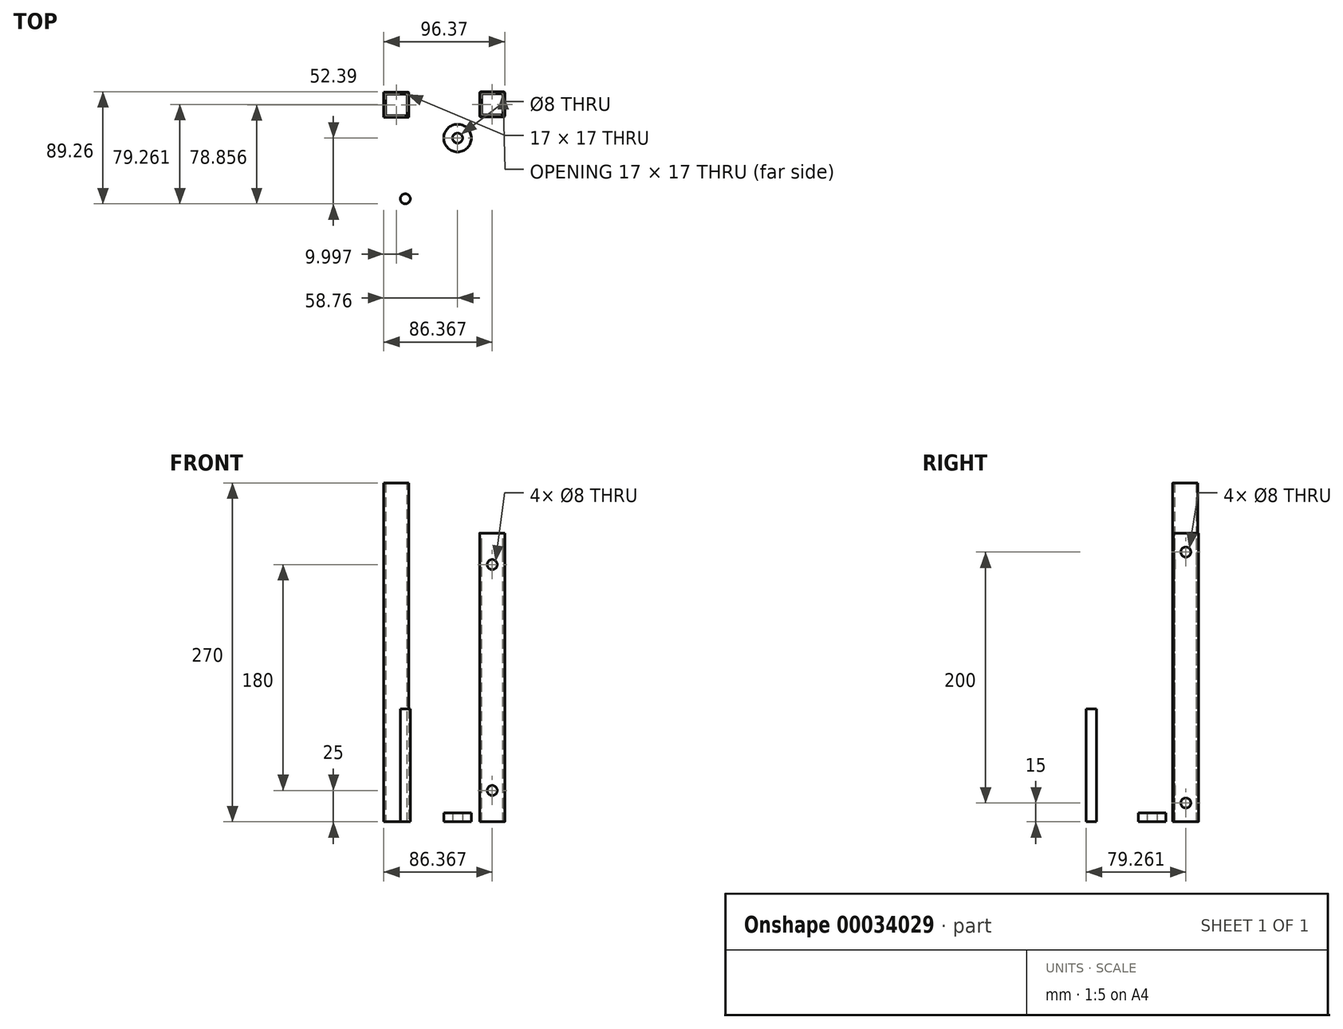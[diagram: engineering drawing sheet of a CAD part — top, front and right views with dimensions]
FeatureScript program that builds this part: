
annotation { "Feature Type Name" : "Feature", "Feature Type Description" : "" }
export const myFeature = defineFeature(function(context is Context, id is Id, definition is map)
    precondition{}
    {
        {
            assignVariable(context, id + "F0", {"name" : "OD1", "anyValue" : 8});
        }
        {
            var Q0;
            Q0=qCreatedBy(makeId("Top.planeOp"),FACE);
            var sketch = newSketch(context, id + "F1", { "sketchPlane" : qUnion([Q0])});
            skCircle(sketch, "E0", {"center": v(0, 0) * mm, "radius": 4 * mm});
            skCircle(sketch, "E1", {"center": v(0, 0) * mm, "radius": 11 * mm});
            skSolve(sketch);
        }
        {
            var Q0;
            Q0 = qSketchRegion(id + "F1", true);
            extrude(context, id + "F2", {"entities" : qUnion([Q0]), "depth" : 7 * mm});
        }
        {
            var Q0;
            Q0=qCreatedBy(makeId("Top.planeOp"),FACE);
            var sketch = newSketch(context, id + "F3", { "sketchPlane" : qUnion([Q0])});
            skLineSegment(sketch, "E2.bottom", {"start": v(-58.76, 36.47) * mm, "end": v(-38.76, 36.47) * mm});
            skLineSegment(sketch, "E2.top", {"start": v(-58.76, 16.47) * mm, "end": v(-38.76, 16.47) * mm});
            skLineSegment(sketch, "E2.left", {"start": v(-58.76, 36.47) * mm, "end": v(-58.76, 16.47) * mm});
            skLineSegment(sketch, "E2.right", {"start": v(-38.76, 36.47) * mm, "end": v(-38.76, 16.47) * mm});
            skSolve(sketch);
        }
        {
            var Q0;
            Q0 = qSketchRegion(id + "F3", true);
            extrude(context, id + "F4", {"entities" : qUnion([Q0]), "depth" : 270 * mm});
        }
        {
            var Q0;
            Q0=makeQuery(id+"F4.opExtrude","SWEPT_EDGE",EDGE,{"disambiguationData":[OSD([sQuery(id+"F3.wireOp",EDGE,"E2.bottom"),sQuery(id+"F3.wireOp",EDGE,"E2.right")])]});
            var Q1;
            Q1=makeQuery(id+"F4.opExtrude","SWEPT_EDGE",EDGE,{"disambiguationData":[OSD([sQuery(id+"F3.wireOp",EDGE,"E2.top"),sQuery(id+"F3.wireOp",EDGE,"E2.right")])]});
            fillet(context, id + "F5", {"entities" : qUnion([Q0, Q1]), "radius" : 0.5 * mm, "tangentPropagation" : true, "allowEdgeOverflow" : false});
        }
        {
            var Q0;
            Q0=makeQuery(id+"F4.opExtrude","CAP_FACE",FACE,{"disambiguationData":[OSD([sQuery(id+"F3.wireOp",EDGE,"E2.bottom"),sQuery(id+"F3.wireOp",EDGE,"E2.top"),sQuery(id+"F3.wireOp",EDGE,"E2.left"),sQuery(id+"F3.wireOp",EDGE,"E2.right")])],"isStart":false});
            var Q1;
            Q1=makeQuery(id+"F4.opExtrude","CAP_FACE",FACE,{"disambiguationData":[OSD([sQuery(id+"F3.wireOp",EDGE,"E2.bottom"),sQuery(id+"F3.wireOp",EDGE,"E2.top"),sQuery(id+"F3.wireOp",EDGE,"E2.left"),sQuery(id+"F3.wireOp",EDGE,"E2.right")])],"isStart":true});
            shell(context, id + "F6", {"entities" : qUnion([Q0, Q1]), "thickness" : 1.5 * mm});
        }
        {
            var Q0;
            Q0=qCreatedBy(makeId("Top.planeOp"),FACE);
            var sketch = newSketch(context, id + "F7", { "sketchPlane" : qUnion([Q0])});
            skLineSegment(sketch, "E3.bottom", {"start": v(17.6, 36.87) * mm, "end": v(37.6, 36.87) * mm});
            skLineSegment(sketch, "E3.top", {"start": v(17.6, 16.87) * mm, "end": v(37.6, 16.87) * mm});
            skLineSegment(sketch, "E3.left", {"start": v(17.6, 36.87) * mm, "end": v(17.6, 16.87) * mm});
            skLineSegment(sketch, "E3.right", {"start": v(37.6, 36.87) * mm, "end": v(37.6, 16.87) * mm});
            skSolve(sketch);
        }
        {
            var Q0;
            Q0 = qSketchRegion(id + "F7", true);
            extrude(context, id + "F8", {"entities" : qUnion([Q0]), "depth" : 230 * mm});
        }
        {
            var Q0;
            Q0=makeQuery(id+"F8.opExtrude","SWEPT_EDGE",EDGE,{"disambiguationData":[OSD([sQuery(id+"F7.wireOp",EDGE,"E3.bottom"),sQuery(id+"F7.wireOp",EDGE,"E3.right")])]});
            var Q1;
            Q1=makeQuery(id+"F8.opExtrude","SWEPT_EDGE",EDGE,{"disambiguationData":[OSD([sQuery(id+"F7.wireOp",EDGE,"E3.bottom"),sQuery(id+"F7.wireOp",EDGE,"E3.left")])]});
            var Q2;
            Q2=makeQuery(id+"F8.opExtrude","SWEPT_EDGE",EDGE,{"disambiguationData":[OSD([sQuery(id+"F7.wireOp",EDGE,"E3.top"),sQuery(id+"F7.wireOp",EDGE,"E3.right")])]});
            var Q3;
            Q3=makeQuery(id+"F8.opExtrude","SWEPT_EDGE",EDGE,{"disambiguationData":[OSD([sQuery(id+"F7.wireOp",EDGE,"E3.top"),sQuery(id+"F7.wireOp",EDGE,"E3.left")])]});
            fillet(context, id + "F9", {"entities" : qUnion([Q0, Q1, Q2, Q3]), "radius" : 1 * mm, "tangentPropagation" : true, "allowEdgeOverflow" : false});
        }
        {
            var Q0;
            Q0=makeQuery(id+"F8.opExtrude","CAP_FACE",FACE,{"disambiguationData":[OSD([sQuery(id+"F7.wireOp",EDGE,"E3.bottom"),sQuery(id+"F7.wireOp",EDGE,"E3.top"),sQuery(id+"F7.wireOp",EDGE,"E3.left"),sQuery(id+"F7.wireOp",EDGE,"E3.right")])],"isStart":false});
            var Q1;
            Q1=makeQuery(id+"F8.opExtrude","CAP_FACE",FACE,{"disambiguationData":[OSD([sQuery(id+"F7.wireOp",EDGE,"E3.bottom"),sQuery(id+"F7.wireOp",EDGE,"E3.top"),sQuery(id+"F7.wireOp",EDGE,"E3.left"),sQuery(id+"F7.wireOp",EDGE,"E3.right")])],"isStart":true});
            shell(context, id + "F10", {"entities" : qUnion([Q0, Q1]), "thickness" : 1.5 * mm});
        }
        {
            var Q0;
            Q0=makeQuery(id+"F8.opExtrude","SWEPT_FACE",FACE,{"disambiguationData":[OSD([sQuery(id+"F7.wireOp",EDGE,"E3.right")])]});
            var sketch = newSketch(context, id + "F11", { "sketchPlane" : qUnion([Q0])});
            skPoint(sketch, "E4", {"position": v(26.87, 215) * mm});
            skPoint(sketch, "E4.positionSnap0", {"position": v(26.87, 230) * mm});
            skPoint(sketch, "E5", {"position": v(26.87, 15) * mm});
            skPoint(sketch, "E5.positionSnap0", {"position": v(26.87, 0) * mm});
            skSolve(sketch);
        }
        {
            var Q0;
            Q0=sQuery(id+"F11.wireOp",VERTEX,"E5");
            var Q1;
            Q1=sQuery(id+"F11.wireOp",VERTEX,"E4");
            var Q2;
            Q2=makeQuery(id+"F8.opExtrude","SWEPT_BODY",BODY,{"disambiguationData":[OSD([sQuery(id+"F7.wireOp",EDGE,"E3.bottom"),sQuery(id+"F7.wireOp",EDGE,"E3.top"),sQuery(id+"F7.wireOp",EDGE,"E3.left"),sQuery(id+"F7.wireOp",EDGE,"E3.right")])]});
            hole(context, id + "F12", {"style" : HoleStyle.SIMPLE, "holeDiameter" : (getVariable(context, 'OD1')) * mm, "endStyle" : HoleEndStyle.THROUGH, "locations" : qUnion([Q0, Q1]), "scope" : qUnion([Q2])});
        }
        {
            var Q0;
            Q0=makeQuery(id+"F8.opExtrude","SWEPT_FACE",FACE,{"disambiguationData":[OSD([sQuery(id+"F7.wireOp",EDGE,"E3.bottom")])]});
            var sketch = newSketch(context, id + "F13", { "sketchPlane" : qUnion([Q0])});
            skPoint(sketch, "E6", {"position": v(-27.6, 25) * mm});
            skPoint(sketch, "E6.positionSnap0", {"position": v(-27.6, 0) * mm});
            skPoint(sketch, "E7", {"position": v(-27.6, 205) * mm});
            skPoint(sketch, "E7.positionSnap0", {"position": v(-27.6, 230) * mm});
            skSolve(sketch);
        }
        {
            var Q0;
            Q0=sQuery(id+"F13.wireOp",VERTEX,"E7");
            var Q1;
            Q1=sQuery(id+"F13.wireOp",VERTEX,"E6");
            var Q2;
            Q2=makeQuery(id+"F8.opExtrude","SWEPT_BODY",BODY,{"disambiguationData":[OSD([sQuery(id+"F7.wireOp",EDGE,"E3.bottom"),sQuery(id+"F7.wireOp",EDGE,"E3.top"),sQuery(id+"F7.wireOp",EDGE,"E3.left"),sQuery(id+"F7.wireOp",EDGE,"E3.right")])]});
            hole(context, id + "F14", {"style" : HoleStyle.SIMPLE, "holeDiameter" : (getVariable(context, 'OD1')) * mm, "endStyle" : HoleEndStyle.THROUGH, "locations" : qUnion([Q0, Q1]), "scope" : qUnion([Q2])});
        }
        {
            var Q0;
            Q0=qCreatedBy(makeId("Top.planeOp"),FACE);
            var sketch = newSketch(context, id + "F15", { "sketchPlane" : qUnion([Q0])});
            skCircle(sketch, "E8", {"center": v(-41.64, -48.39) * mm, "radius": 4 * mm});
            skSolve(sketch);
        }
        {
            var Q0;
            Q0 = qSketchRegion(id + "F15", true);
            extrude(context, id + "F16", {"entities" : qUnion([Q0]), "depth" : 90 * mm});
        }
        {
            var Q0;
            Q0=makeQuery(id+"F10.opShell","OFFSET_EDGE",EDGE,{"disambiguationData":[OSD([sQuery(id+"F7.wireOp",EDGE,"E3.top"),sQuery(id+"F7.wireOp",EDGE,"E3.left")])]});
            var Q1;
            Q1=makeQuery(id+"F10.opShell","OFFSET_EDGE",EDGE,{"disambiguationData":[OSD([sQuery(id+"F7.wireOp",EDGE,"E3.top"),sQuery(id+"F7.wireOp",EDGE,"E3.right")])]});
            var Q2;
            Q2=makeQuery(id+"F10.opShell","OFFSET_EDGE",EDGE,{"disambiguationData":[OSD([sQuery(id+"F7.wireOp",EDGE,"E3.bottom"),sQuery(id+"F7.wireOp",EDGE,"E3.right")])]});
            var Q3;
            Q3=makeQuery(id+"F10.opShell","OFFSET_EDGE",EDGE,{"disambiguationData":[OSD([sQuery(id+"F7.wireOp",EDGE,"E3.bottom"),sQuery(id+"F7.wireOp",EDGE,"E3.left")])]});
            fillet(context, id + "F17", {"entities" : qUnion([Q0, Q1, Q2, Q3]), "radius" : 0.5 * mm, "tangentPropagation" : true, "allowEdgeOverflow" : false});
        }
    });
